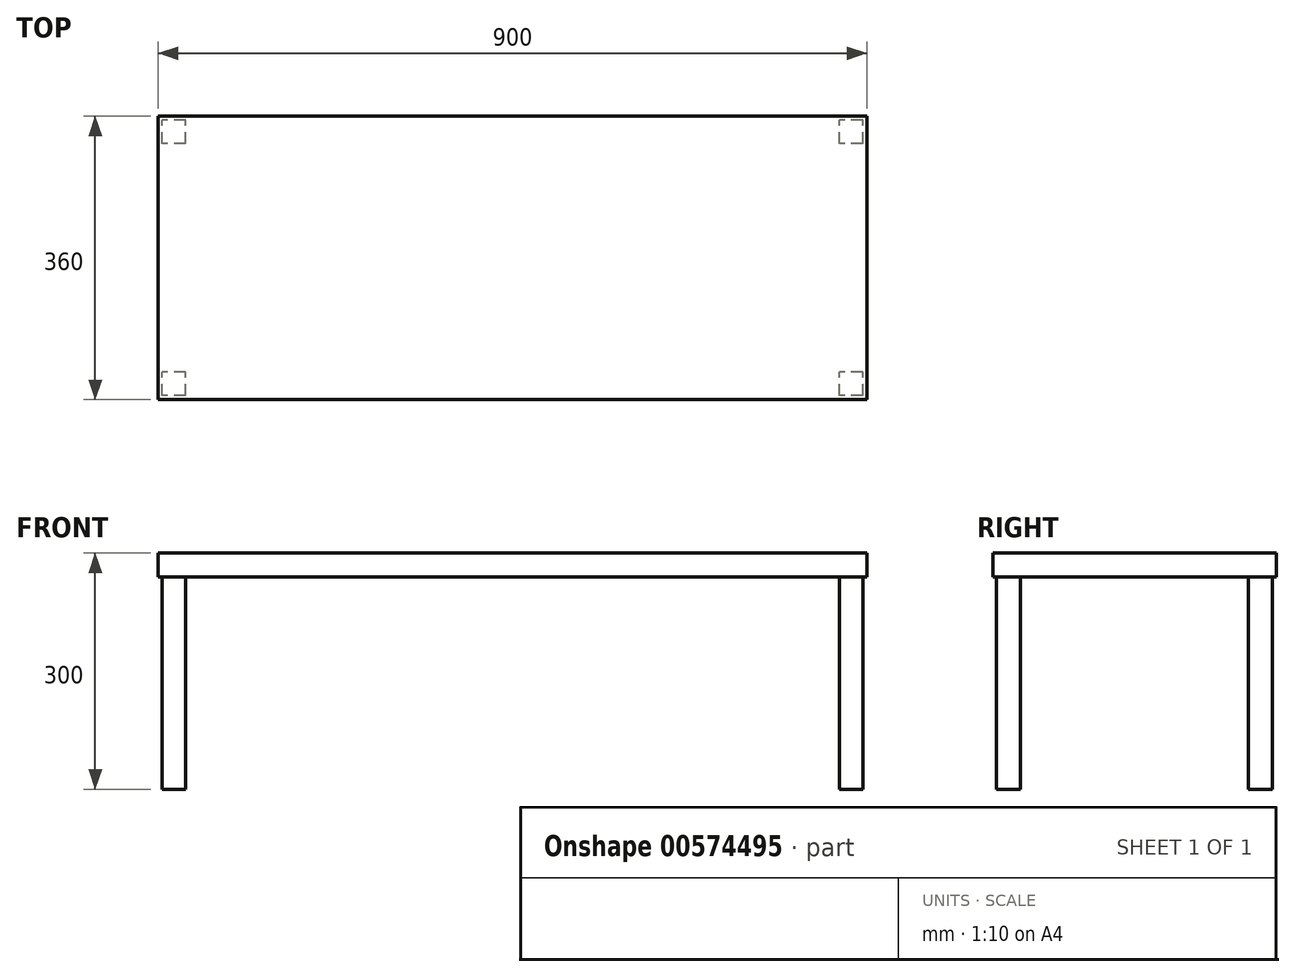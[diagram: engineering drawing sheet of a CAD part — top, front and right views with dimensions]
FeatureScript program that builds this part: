
annotation { "Feature Type Name" : "Feature", "Feature Type Description" : "" }
export const myFeature = defineFeature(function(context is Context, id is Id, definition is map)
    precondition{}
    {
        {
            var Q0;
            Q0=qCreatedBy(makeId("Top.planeOp"),FACE);
            var sketch = newSketch(context, id + "F0", { "sketchPlane" : qUnion([Q0])});
            skLineSegment(sketch, "E0.bottom", {"start": v(450, 180) * mm, "end": v(-450, 180) * mm});
            skLineSegment(sketch, "E0.top", {"start": v(450, -180) * mm, "end": v(-450, -180) * mm});
            skLineSegment(sketch, "E0.left", {"start": v(450, 180) * mm, "end": v(450, -180) * mm});
            skLineSegment(sketch, "E0.right", {"start": v(-450, 180) * mm, "end": v(-450, -180) * mm});
            skPoint(sketch, "E0.middle", {"position": v(0, 0) * mm});
            skSolve(sketch);
        }
        {
            var Q0;
            Q0 = qSketchRegion(id + "F0", true);
            extrude(context, id + "F1", {"entities" : qUnion([Q0]), "depth" : 30 * mm, "offsetDistance" : 25 * mm});
        }
        {
            var Q0;
            Q0=makeQuery(id+"F1.opExtrude","CAP_FACE",FACE,{"disambiguationData":[OSD([sQuery(id+"F0.wireOp",EDGE,"E0.bottom"),sQuery(id+"F0.wireOp",EDGE,"E0.top"),sQuery(id+"F0.wireOp",EDGE,"E0.left"),sQuery(id+"F0.wireOp",EDGE,"E0.right")])],"isStart":true});
            var sketch = newSketch(context, id + "F2", { "sketchPlane" : qUnion([Q0])});
            skLineSegment(sketch, "E1.bottom", {"start": v(-415, 175) * mm, "end": v(-445, 175) * mm});
            skLineSegment(sketch, "E1.top", {"start": v(-415, 145) * mm, "end": v(-445, 145) * mm});
            skLineSegment(sketch, "E1.left", {"start": v(-415, 175) * mm, "end": v(-415, 145) * mm});
            skLineSegment(sketch, "E1.right", {"start": v(-445, 175) * mm, "end": v(-445, 145) * mm});
            skPoint(sketch, "E1.middle", {"position": v(-430, 160) * mm});
            skLineSegment(sketch, "E2.bottom", {"start": v(445, 175) * mm, "end": v(415, 175) * mm});
            skLineSegment(sketch, "E2.top", {"start": v(445, 145) * mm, "end": v(415, 145) * mm});
            skLineSegment(sketch, "E2.left", {"start": v(445, 175) * mm, "end": v(445, 145) * mm});
            skLineSegment(sketch, "E2.right", {"start": v(415, 175) * mm, "end": v(415, 145) * mm});
            skPoint(sketch, "E2.middle", {"position": v(430, 160) * mm});
            skLineSegment(sketch, "E3.bottom", {"start": v(445, -145) * mm, "end": v(415, -145) * mm});
            skLineSegment(sketch, "E3.top", {"start": v(445, -175) * mm, "end": v(415, -175) * mm});
            skLineSegment(sketch, "E3.left", {"start": v(445, -145) * mm, "end": v(445, -175) * mm});
            skLineSegment(sketch, "E3.right", {"start": v(415, -145) * mm, "end": v(415, -175) * mm});
            skPoint(sketch, "E3.middle", {"position": v(430, -160) * mm});
            skLineSegment(sketch, "E4.bottom", {"start": v(-415, -145) * mm, "end": v(-445, -145) * mm});
            skLineSegment(sketch, "E4.top", {"start": v(-415, -175) * mm, "end": v(-445, -175) * mm});
            skLineSegment(sketch, "E4.left", {"start": v(-415, -145) * mm, "end": v(-415, -175) * mm});
            skLineSegment(sketch, "E4.right", {"start": v(-445, -145) * mm, "end": v(-445, -175) * mm});
            skPoint(sketch, "E4.middle", {"position": v(-430, -160) * mm});
            skSolve(sketch);
        }
        {
            var Q0;
            Q0 = qSketchRegion(id + "F2", true);
            extrude(context, id + "F3", {"entities" : qUnion([Q0]), "operationType" : NewBodyOperationType.ADD, "depth" : 270 * mm, "offsetDistance" : 25 * mm});
        }
    });
